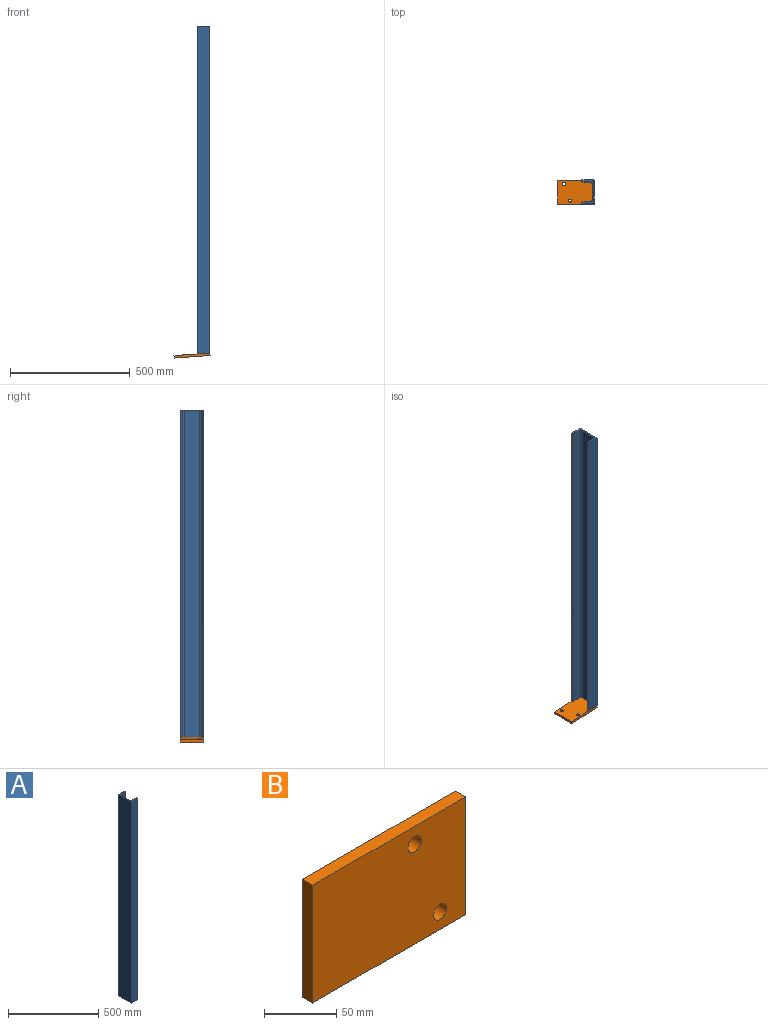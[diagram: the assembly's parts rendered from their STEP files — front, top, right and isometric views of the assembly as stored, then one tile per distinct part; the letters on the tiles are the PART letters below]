
ASSEMBLY  parts=2 mates=1
PART A: 14 faces, bbox 50x100x1369.4 mm
  f0: plane 1369.36x50mm, normal (0,1,0), area 68382.2mm2, adj f9,f10,f12,f13
  f1: cylinder r=4.5mm len=1369.36mm, axis (0,0,1), area 9678.6mm2, adj f2,f10,f12,f13
  f2: plane 1369.05x31mm, normal (0.06,-1,0), area 42495.8mm2, adj f1,f3,f12,f13
  f3: cylinder r=8.5mm len=1366.92mm, axis (0,0,1), area 18245.9mm2, adj f2,f4,f12,f13
  f4: plane 1366.34x64mm, normal (1,0,0), area 87445.8mm2, adj f3,f5,f12,f13
  f5: cylinder r=8.5mm len=1366.92mm, axis (0,0,1), area 18245.9mm2, adj f4,f6,f12,f13
  f6: plane 1369.05x31mm, normal (0.06,1,0), area 42495.8mm2, adj f5,f7,f12,f13
  f7: cylinder r=4.5mm len=1369.36mm, axis (0,0,1), area 9678.6mm2, adj f6,f11,f12,f13
  f8: plane 1369.36x50mm, normal (0,-1,0), area 68382.2mm2, adj f9,f11,f12,f13
  f9: plane 1365.93x100mm, normal (-1,0,0), area 136592.9mm2, adj f0,f8,f12,f13
  f10: plane 1369.36x3mm, normal (1,0,0), area 4108.1mm2, adj f0,f1,f12,f13
  f11: plane 1369.36x3mm, normal (1,0,0), area 4108.1mm2, adj f7,f8,f12,f13
  f12: plane 100x50mm, normal (0,0,1), area 1378.3mm2, adj f0,f1,f2,f3,f4,f5,f6,f7
  f13: plane 100x50mm, normal (-0.07,0,-1), area 1381.6mm2, adj f0,f1,f2,f3,f4,f5,f6,f7
PART B: 8 faces, bbox 150x10x100 mm
  f0: plane 150x10mm, normal (0,0,-1), area 1500mm2, adj f1,f5,f6,f7
  f1: plane 100x10mm, normal (1,0,0), area 1000mm2, adj f0,f2,f6,f7
  f2: plane 150x10mm, normal (0,0,1), area 1500mm2, adj f1,f5,f6,f7
  f3: cylinder r=6.5mm len=13mm, axis (0,1,0), area 408.4mm2, adj f6,f7
  f4: cylinder r=6.5mm len=13mm, axis (0,1,0), area 408.4mm2, adj f6,f7
  f5: plane 100x10mm, normal (-1,0,0), area 1000mm2, adj f0,f2,f6,f7
  f6: plane 150x100mm, normal (0,-1,0), area 14734.5mm2, adj f0,f1,f2,f3,f4,f5
  f7: plane 150x100mm, normal (0,1,0), area 14734.5mm2, adj f0,f1,f2,f3,f4,f5
PLACE A rot(axis=(0,0,1),180deg) t=(-15.38,71.78,-565.87)mm
PLACE B rot(axis=(0.02,0.71,-0.71),177.2deg) t=(-89.88,21.71,-572.57)mm
MATE fastened B.f6 <-> A.f13  axis (-0.07,0,1) through (-15.4,21.71,-562.44)mm
